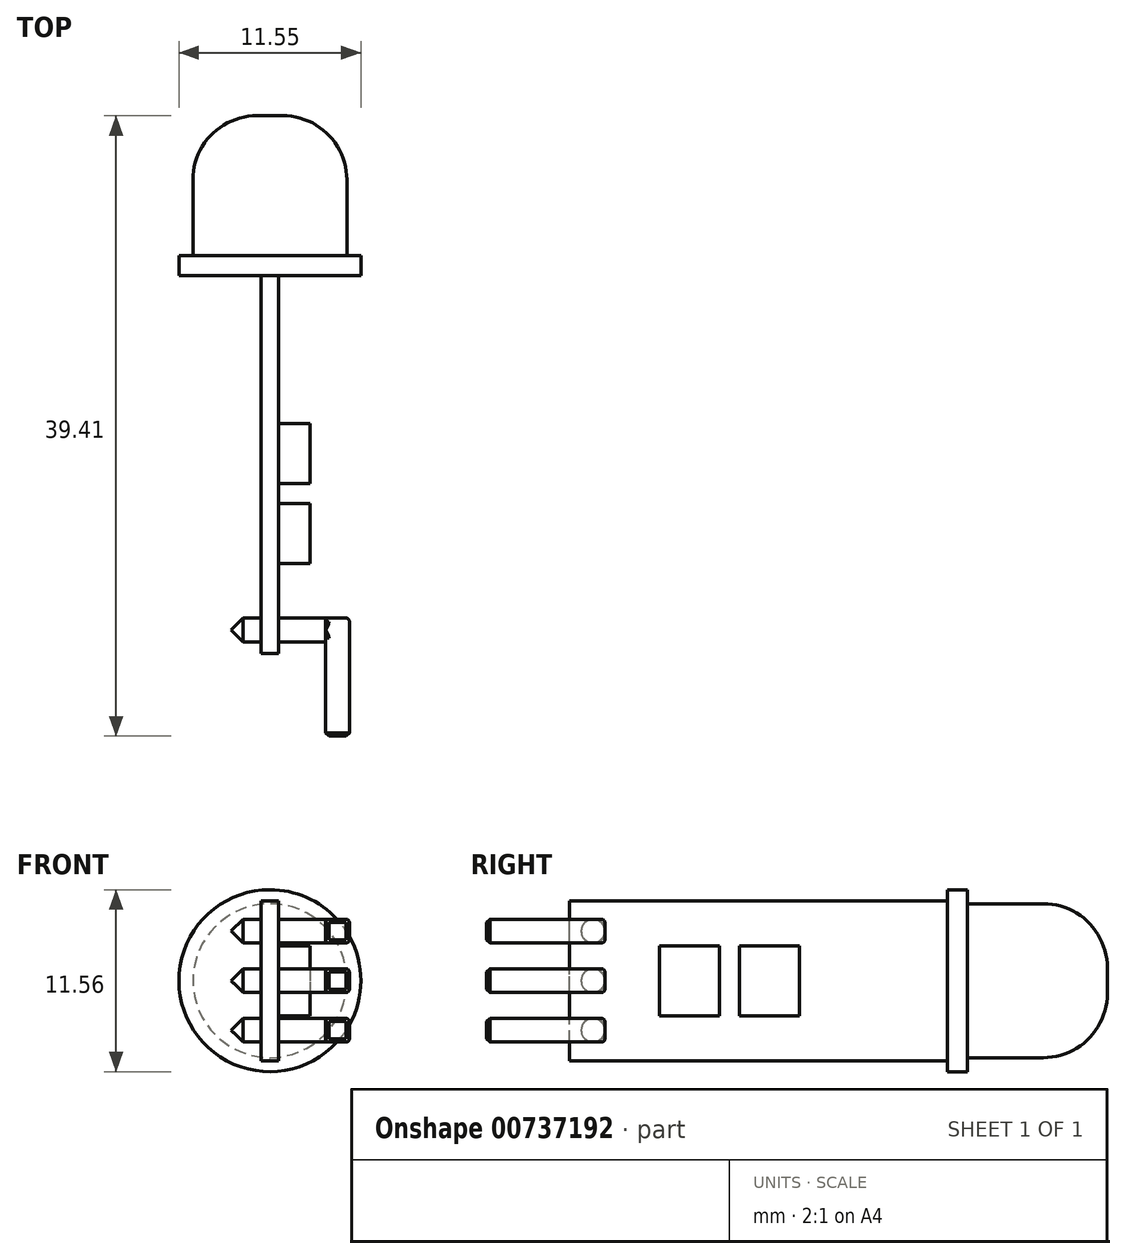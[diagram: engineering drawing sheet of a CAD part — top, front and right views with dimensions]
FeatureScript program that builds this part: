
annotation { "Feature Type Name" : "Feature", "Feature Type Description" : "" }
export const myFeature = defineFeature(function(context is Context, id is Id, definition is map)
    precondition{}
    {
        {
            var Q0;
            Q0=qCreatedBy(makeId("Right.planeOp"),FACE);
            var sketch = newSketch(context, id + "F0", { "sketchPlane" : qUnion([Q0])});
            skLineSegment(sketch, "E0.bottom", {"start": v(12, -5.08) * mm, "end": v(-12, -5.08) * mm});
            skLineSegment(sketch, "E0.top", {"start": v(12, 5.08) * mm, "end": v(-12, 5.08) * mm});
            skLineSegment(sketch, "E0.left", {"start": v(12, -5.08) * mm, "end": v(12, 5.08) * mm});
            skLineSegment(sketch, "E0.right", {"start": v(-12, -5.08) * mm, "end": v(-12, 5.08) * mm});
            skPoint(sketch, "E0.middle", {"position": v(0, 0) * mm});
            skSolve(sketch);
        }
        {
            var Q0;
            Q0 = qSketchRegion(id + "F0", true);
            extrude(context, id + "F1", {"entities" : qUnion([Q0]), "depth" : 1.1 * mm, "offsetDistance" : 25.4 * mm});
        }
        {
            var Q0;
            Q0=makeQuery(id+"F1.opExtrude","SWEPT_FACE",FACE,{"disambiguationData":[OSD([sQuery(id+"F0.wireOp",EDGE,"E0.left")])]});
            var sketch = newSketch(context, id + "F2", { "sketchPlane" : qUnion([Q0])});
            skLineSegment(sketch, "E1", {"start": v(-0.55, 5.08) * mm, "end": v(-0.55, -5.08) * mm});
            skCircle(sketch, "E2", {"center": v(-0.55, 0) * mm, "radius": 5.78 * mm});
            skSolve(sketch);
        }
        {
            var Q0;
            Q0 = qSketchRegion(id + "F2", true);
            extrude(context, id + "F3", {"entities" : qUnion([Q0]), "operationType" : NewBodyOperationType.ADD, "depth" : 1.27 * mm, "offsetDistance" : 25.4 * mm});
        }
        {
            var Q0;
            Q0=makeQuery(id+"F3.opExtrude","CAP_FACE",FACE,{"disambiguationData":[OSD([sQuery(id+"F2.wireOp",EDGE,"E2")])],"isStart":false});
            var sketch = newSketch(context, id + "F4", { "sketchPlane" : qUnion([Q0])});
            skCircle(sketch, "E3", {"center": v(-0.55, 0) * mm, "radius": 4.89 * mm});
            skSolve(sketch);
        }
        {
            var Q0;
            Q0 = qSketchRegion(id + "F4", true);
            extrude(context, id + "F5", {"entities" : qUnion([Q0]), "operationType" : NewBodyOperationType.ADD, "depth" : 10.16 * mm - 1.27 * mm, "offsetDistance" : 25.4 * mm});
        }
        {
            var Q0;
            Q0=makeQuery(id+"F5.opExtrude","CAP_EDGE",EDGE,{"disambiguationData":[OSD([sQuery(id+"F4.wireOp",EDGE,"E3")])],"isStart":false});
            fillet(context, id + "F6", {"entities" : qUnion([Q0]), "radius" : 4.06 * mm, "tangentPropagation" : true, "allowEdgeOverflow" : false});
        }
        {
            var Q0;
            Q0=makeQuery(id+"F1.opExtrude","CAP_FACE",FACE,{"disambiguationData":[OSD([sQuery(id+"F0.wireOp",EDGE,"E0.bottom"),sQuery(id+"F0.wireOp",EDGE,"E0.top"),sQuery(id+"F0.wireOp",EDGE,"E0.left"),sQuery(id+"F0.wireOp",EDGE,"E0.right")])],"isStart":false});
            var sketch = newSketch(context, id + "F7", { "sketchPlane" : qUnion([Q0])});
            skLineSegment(sketch, "E4.bottom", {"start": v(-2.48, 2.22) * mm, "end": v(-6.29, 2.22) * mm});
            skLineSegment(sketch, "E4.top", {"start": v(-2.48, -2.22) * mm, "end": v(-6.29, -2.22) * mm});
            skLineSegment(sketch, "E4.left", {"start": v(-2.48, 2.22) * mm, "end": v(-2.48, -2.22) * mm});
            skLineSegment(sketch, "E4.right", {"start": v(-6.29, 2.22) * mm, "end": v(-6.29, -2.22) * mm});
            skPoint(sketch, "E4.middle", {"position": v(-4.38, 0) * mm});
            skLineSegment(sketch, "E5.bottom", {"start": v(2.6, 2.22) * mm, "end": v(-1.2, 2.22) * mm});
            skLineSegment(sketch, "E5.top", {"start": v(2.6, -2.22) * mm, "end": v(-1.2, -2.22) * mm});
            skLineSegment(sketch, "E5.left", {"start": v(2.6, 2.22) * mm, "end": v(2.6, -2.22) * mm});
            skLineSegment(sketch, "E5.right", {"start": v(-1.2, 2.22) * mm, "end": v(-1.2, -2.22) * mm});
            skPoint(sketch, "E5.middle", {"position": v(0.7, 0) * mm});
            skSolve(sketch);
        }
        {
            var Q0;
            Q0 = qSketchRegion(id + "F7", true);
            extrude(context, id + "F8", {"entities" : qUnion([Q0]), "operationType" : NewBodyOperationType.ADD, "depth" : 2 * mm, "offsetDistance" : 25.4 * mm});
        }
        {
            var Q0;
            Q0=makeQuery(id+"F1.opExtrude","CAP_FACE",FACE,{"disambiguationData":[OSD([sQuery(id+"F0.wireOp",EDGE,"E0.bottom"),sQuery(id+"F0.wireOp",EDGE,"E0.top"),sQuery(id+"F0.wireOp",EDGE,"E0.left"),sQuery(id+"F0.wireOp",EDGE,"E0.right")])],"isStart":false});
            var sketch = newSketch(context, id + "F9", { "sketchPlane" : qUnion([Q0])});
            skCircle(sketch, "E6", {"center": v(-10.5, 0) * mm, "radius": 0.75 * mm});
            skCircle(sketch, "E7", {"center": v(-10.5, -3.15) * mm, "radius": 0.75 * mm});
            skCircle(sketch, "E8", {"center": v(-10.5, 3.15) * mm, "radius": 0.75 * mm});
            skPoint(sketch, "E9", {"position": v(-12, 0) * mm});
            skSolve(sketch);
        }
        {
            var Q0;
            Q0 = qSketchRegion(id + "F9", true);
            extrude(context, id + "F10", {"entities" : qUnion([Q0]), "operationType" : NewBodyOperationType.ADD, "endBound" : BoundingType.SYMMETRIC, "depth" : 6 * mm, "offsetDistance" : 25.4 * mm});
        }
        {
            var Q0;
            Q0=makeQuery(id+"F10.opExtrude","CAP_EDGE",EDGE,{"disambiguationData":[OSD([sQuery(id+"F9.wireOp",EDGE,"E8")])],"isStart":true});
            var Q1;
            Q1=makeQuery(id+"F10.opExtrude","CAP_EDGE",EDGE,{"disambiguationData":[OSD([sQuery(id+"F9.wireOp",EDGE,"E6")])],"isStart":true});
            var Q2;
            Q2=makeQuery(id+"F10.opExtrude","CAP_EDGE",EDGE,{"disambiguationData":[OSD([sQuery(id+"F9.wireOp",EDGE,"E7")])],"isStart":true});
            chamfer(context, id + "F11", {"entities" : qUnion([Q0, Q1, Q2]), "width" : 0.75 * mm, "tangentPropagation" : true});
        }
        {
            var Q0;
            Q0=makeQuery(id+"F10.opExtrude","CAP_FACE",FACE,{"disambiguationData":[OSD([sQuery(id+"F9.wireOp",EDGE,"E8")])],"isStart":false});
            var sketch = newSketch(context, id + "F12", { "sketchPlane" : qUnion([Q0])});
            skLineSegment(sketch, "E10.bottom", {"start": v(-17.25, 3.9) * mm, "end": v(-9.75, 3.9) * mm});
            skLineSegment(sketch, "E10.top", {"start": v(-17.25, 2.4) * mm, "end": v(-9.75, 2.4) * mm});
            skLineSegment(sketch, "E10.left", {"start": v(-17.25, 3.9) * mm, "end": v(-17.25, 2.4) * mm});
            skLineSegment(sketch, "E10.right", {"start": v(-9.75, 3.9) * mm, "end": v(-9.75, 2.4) * mm});
            skPoint(sketch, "E10.middle", {"position": v(-10.5, 3.15) * mm});
            skLineSegment(sketch, "E11.bottom", {"start": v(-17.25, 0.75) * mm, "end": v(-9.75, 0.75) * mm});
            skLineSegment(sketch, "E11.top", {"start": v(-17.25, -0.75) * mm, "end": v(-9.75, -0.75) * mm});
            skLineSegment(sketch, "E11.left", {"start": v(-17.25, 0.75) * mm, "end": v(-17.25, -0.75) * mm});
            skLineSegment(sketch, "E11.right", {"start": v(-9.75, 0.75) * mm, "end": v(-9.75, -0.75) * mm});
            skPoint(sketch, "E11.middle", {"position": v(-13.5, 0) * mm});
            skLineSegment(sketch, "E12.bottom", {"start": v(-17.25, -2.4) * mm, "end": v(-9.75, -2.4) * mm});
            skLineSegment(sketch, "E12.top", {"start": v(-17.25, -3.9) * mm, "end": v(-9.75, -3.9) * mm});
            skLineSegment(sketch, "E12.left", {"start": v(-17.25, -2.4) * mm, "end": v(-17.25, -3.9) * mm});
            skLineSegment(sketch, "E12.right", {"start": v(-9.75, -2.4) * mm, "end": v(-9.75, -3.9) * mm});
            skPoint(sketch, "E12.middle", {"position": v(-13.5, -3.15) * mm});
            skSolve(sketch);
        }
        {
            var Q0;
            Q0 = qSketchRegion(id + "F12", true);
            extrude(context, id + "F13", {"entities" : qUnion([Q0]), "operationType" : NewBodyOperationType.ADD, "depth" : 1.5 * mm, "offsetDistance" : 25.4 * mm});
        }
        {
            var Q0;
            {var subQ0=sQuery(id+"F12.wireOp",EDGE,"E12.right");var subQ1=sQuery(id+"F12.wireOp",EDGE,"E12.top");var subQ2=makeQuery(id+"F13.opExtrude","CAP_FACE",FACE,{"disambiguationData":[OSD([sQuery(id+"F12.wireOp",EDGE,"E12.bottom"),subQ1,sQuery(id+"F12.wireOp",EDGE,"E12.left"),subQ0])],"isStart":true});Q0=makeQuery(id+"F13.boolean.opBoolean","SPLIT",FACE,{"disambiguationData":[TD([makeQuery(id+"F10.opExtrude","SWEPT_FACE",FACE,{"disambiguationData":[OSD([sQuery(id+"F9.wireOp",EDGE,"E7")])]}),subQ2,makeQuery(id+"F13.opExtrude","SWEPT_FACE",FACE,{"disambiguationData":[OSD([subQ1])]}),makeQuery(id+"F13.opExtrude","SWEPT_FACE",FACE,{"disambiguationData":[OSD([subQ0])]})])],"derivedFrom":subQ2});}
            var Q1;
            {var subQ0=sQuery(id+"F12.wireOp",EDGE,"E12.right");var subQ1=sQuery(id+"F12.wireOp",EDGE,"E12.bottom");var subQ2=makeQuery(id+"F13.opExtrude","CAP_FACE",FACE,{"disambiguationData":[OSD([subQ1,sQuery(id+"F12.wireOp",EDGE,"E12.top"),sQuery(id+"F12.wireOp",EDGE,"E12.left"),subQ0])],"isStart":true});Q1=makeQuery(id+"F13.boolean.opBoolean","SPLIT",FACE,{"disambiguationData":[TD([makeQuery(id+"F10.opExtrude","SWEPT_FACE",FACE,{"disambiguationData":[OSD([sQuery(id+"F9.wireOp",EDGE,"E7")])]}),makeQuery(id+"F13.opExtrude","SWEPT_FACE",FACE,{"disambiguationData":[OSD([subQ1])]}),subQ2,makeQuery(id+"F13.opExtrude","SWEPT_FACE",FACE,{"disambiguationData":[OSD([subQ0])]})])],"derivedFrom":subQ2});}
            var Q2;
            {var subQ0=sQuery(id+"F12.wireOp",EDGE,"E11.right");var subQ1=sQuery(id+"F12.wireOp",EDGE,"E11.top");var subQ2=makeQuery(id+"F13.opExtrude","CAP_FACE",FACE,{"disambiguationData":[OSD([sQuery(id+"F12.wireOp",EDGE,"E11.bottom"),subQ1,sQuery(id+"F12.wireOp",EDGE,"E11.left"),subQ0])],"isStart":true});Q2=makeQuery(id+"F13.boolean.opBoolean","SPLIT",FACE,{"disambiguationData":[TD([makeQuery(id+"F10.opExtrude","SWEPT_FACE",FACE,{"disambiguationData":[OSD([sQuery(id+"F9.wireOp",EDGE,"E6")])]}),subQ2,makeQuery(id+"F13.opExtrude","SWEPT_FACE",FACE,{"disambiguationData":[OSD([subQ1])]}),makeQuery(id+"F13.opExtrude","SWEPT_FACE",FACE,{"disambiguationData":[OSD([subQ0])]})])],"derivedFrom":subQ2});}
            var Q3;
            {var subQ0=sQuery(id+"F12.wireOp",EDGE,"E11.bottom");var subQ1=sQuery(id+"F12.wireOp",EDGE,"E11.right");var subQ2=makeQuery(id+"F13.opExtrude","CAP_FACE",FACE,{"disambiguationData":[OSD([subQ0,sQuery(id+"F12.wireOp",EDGE,"E11.top"),sQuery(id+"F12.wireOp",EDGE,"E11.left"),subQ1])],"isStart":true});Q3=makeQuery(id+"F13.boolean.opBoolean","SPLIT",FACE,{"disambiguationData":[TD([makeQuery(id+"F10.opExtrude","SWEPT_FACE",FACE,{"disambiguationData":[OSD([sQuery(id+"F9.wireOp",EDGE,"E6")])]}),makeQuery(id+"F13.opExtrude","SWEPT_FACE",FACE,{"disambiguationData":[OSD([subQ0])]}),subQ2,makeQuery(id+"F13.opExtrude","SWEPT_FACE",FACE,{"disambiguationData":[OSD([subQ1])]})])],"derivedFrom":subQ2});}
            var Q4;
            {var subQ0=sQuery(id+"F12.wireOp",EDGE,"E10.right");var subQ1=sQuery(id+"F12.wireOp",EDGE,"E10.top");var subQ2=makeQuery(id+"F13.opExtrude","CAP_FACE",FACE,{"disambiguationData":[OSD([sQuery(id+"F12.wireOp",EDGE,"E10.bottom"),subQ1,sQuery(id+"F12.wireOp",EDGE,"E10.left"),subQ0])],"isStart":true});Q4=makeQuery(id+"F13.boolean.opBoolean","SPLIT",FACE,{"disambiguationData":[TD([makeQuery(id+"F10.opExtrude","SWEPT_FACE",FACE,{"disambiguationData":[OSD([sQuery(id+"F9.wireOp",EDGE,"E8")])]}),subQ2,makeQuery(id+"F13.opExtrude","SWEPT_FACE",FACE,{"disambiguationData":[OSD([subQ1])]}),makeQuery(id+"F13.opExtrude","SWEPT_FACE",FACE,{"disambiguationData":[OSD([subQ0])]})])],"derivedFrom":subQ2});}
            var Q5;
            {var subQ0=sQuery(id+"F12.wireOp",EDGE,"E10.right");var subQ1=sQuery(id+"F12.wireOp",EDGE,"E10.bottom");var subQ2=makeQuery(id+"F13.opExtrude","CAP_FACE",FACE,{"disambiguationData":[OSD([subQ1,sQuery(id+"F12.wireOp",EDGE,"E10.top"),sQuery(id+"F12.wireOp",EDGE,"E10.left"),subQ0])],"isStart":true});Q5=makeQuery(id+"F13.boolean.opBoolean","SPLIT",FACE,{"disambiguationData":[TD([makeQuery(id+"F10.opExtrude","SWEPT_FACE",FACE,{"disambiguationData":[OSD([sQuery(id+"F9.wireOp",EDGE,"E8")])]}),makeQuery(id+"F13.opExtrude","SWEPT_FACE",FACE,{"disambiguationData":[OSD([subQ1])]}),subQ2,makeQuery(id+"F13.opExtrude","SWEPT_FACE",FACE,{"disambiguationData":[OSD([subQ0])]})])],"derivedFrom":subQ2});}
            extrude(context, id + "F14", {"entities" : qUnion([Q0, Q1, Q2, Q3, Q4, Q5]), "operationType" : NewBodyOperationType.ADD, "oppositeDirection" : true, "depth" : 1.5 * mm, "offsetDistance" : 25.4 * mm});
        }
        {
            var Q0;
            Q0=makeQuery(id+"F13.opExtrude","SWEPT_EDGE",EDGE,{"disambiguationData":[OSD([sQuery(id+"F12.wireOp",EDGE,"E12.top"),sQuery(id+"F12.wireOp",EDGE,"E12.right")])]});
            var Q1;
            Q1=makeQuery(id+"F13.opExtrude","CAP_EDGE",EDGE,{"disambiguationData":[OSD([sQuery(id+"F12.wireOp",EDGE,"E12.top")])],"isStart":false});
            var Q2;
            {var subQ0=sQuery(id+"F12.wireOp",EDGE,"E12.left");var subQ1=sQuery(id+"F12.wireOp",EDGE,"E12.top");Q2=makeQuery(id+"F13.boolean.opBoolean","SPLIT",EDGE,{"disambiguationData":[TD([makeQuery(id+"F13.opExtrude","SWEPT_FACE",FACE,{"disambiguationData":[OSD([subQ0])]})])],"derivedFrom":makeQuery(id+"F13.opExtrude","CAP_EDGE",EDGE,{"disambiguationData":[OSD([subQ1])],"isStart":true})});}
            var Q3;
            {var subQ0=sQuery(id+"F12.wireOp",EDGE,"E12.right");var subQ1=sQuery(id+"F12.wireOp",EDGE,"E12.top");Q3=makeQuery(id+"F13.boolean.opBoolean","SPLIT",EDGE,{"disambiguationData":[TD([makeQuery(id+"F13.opExtrude","SWEPT_FACE",FACE,{"disambiguationData":[OSD([subQ0])]})])],"derivedFrom":makeQuery(id+"F13.opExtrude","CAP_EDGE",EDGE,{"disambiguationData":[OSD([subQ1])],"isStart":true})});}
            var Q4;
            {var subQ0=sQuery(id+"F12.wireOp",EDGE,"E12.right");var subQ1=sQuery(id+"F12.wireOp",EDGE,"E12.top");Q4=makeQuery(id+"F13.boolean.opBoolean","SPLIT",EDGE,{"disambiguationData":[TD([makeQuery(id+"F13.opExtrude","SWEPT_FACE",FACE,{"disambiguationData":[OSD([subQ1])]})])],"derivedFrom":makeQuery(id+"F13.opExtrude","CAP_EDGE",EDGE,{"disambiguationData":[OSD([subQ0])],"isStart":true})});}
            var Q5;
            {var subQ0=sQuery(id+"F12.wireOp",EDGE,"E12.right");var subQ1=sQuery(id+"F12.wireOp",EDGE,"E12.bottom");Q5=makeQuery(id+"F13.boolean.opBoolean","SPLIT",EDGE,{"disambiguationData":[TD([makeQuery(id+"F13.opExtrude","SWEPT_FACE",FACE,{"disambiguationData":[OSD([subQ1])]})])],"derivedFrom":makeQuery(id+"F13.opExtrude","CAP_EDGE",EDGE,{"disambiguationData":[OSD([subQ0])],"isStart":true})});}
            var Q6;
            Q6=makeQuery(id+"F13.opExtrude","SWEPT_EDGE",EDGE,{"disambiguationData":[OSD([sQuery(id+"F12.wireOp",EDGE,"E12.bottom"),sQuery(id+"F12.wireOp",EDGE,"E12.right")])]});
            var Q7;
            Q7=makeQuery(id+"F13.opExtrude","CAP_EDGE",EDGE,{"disambiguationData":[OSD([sQuery(id+"F12.wireOp",EDGE,"E12.right")])],"isStart":false});
            var Q8;
            Q8=makeQuery(id+"F13.opExtrude","CAP_EDGE",EDGE,{"disambiguationData":[OSD([sQuery(id+"F12.wireOp",EDGE,"E12.bottom")])],"isStart":false});
            var Q9;
            {var subQ0=sQuery(id+"F12.wireOp",EDGE,"E12.left");var subQ1=sQuery(id+"F12.wireOp",EDGE,"E12.bottom");Q9=makeQuery(id+"F13.boolean.opBoolean","SPLIT",EDGE,{"disambiguationData":[TD([makeQuery(id+"F13.opExtrude","SWEPT_FACE",FACE,{"disambiguationData":[OSD([subQ0])]})])],"derivedFrom":makeQuery(id+"F13.opExtrude","CAP_EDGE",EDGE,{"disambiguationData":[OSD([subQ1])],"isStart":true})});}
            var Q10;
            {var subQ0=sQuery(id+"F12.wireOp",EDGE,"E12.right");var subQ1=sQuery(id+"F12.wireOp",EDGE,"E12.bottom");Q10=makeQuery(id+"F13.boolean.opBoolean","SPLIT",EDGE,{"disambiguationData":[TD([makeQuery(id+"F13.opExtrude","SWEPT_FACE",FACE,{"disambiguationData":[OSD([subQ0])]})])],"derivedFrom":makeQuery(id+"F13.opExtrude","CAP_EDGE",EDGE,{"disambiguationData":[OSD([subQ1])],"isStart":true})});}
            var Q11;
            {var subQ0=sQuery(id+"F12.wireOp",EDGE,"E11.bottom");var subQ1=sQuery(id+"F12.wireOp",EDGE,"E11.right");Q11=makeQuery(id+"F13.boolean.opBoolean","SPLIT",EDGE,{"disambiguationData":[TD([makeQuery(id+"F13.opExtrude","SWEPT_FACE",FACE,{"disambiguationData":[OSD([subQ1])]})])],"derivedFrom":makeQuery(id+"F13.opExtrude","CAP_EDGE",EDGE,{"disambiguationData":[OSD([subQ0])],"isStart":true})});}
            var Q12;
            {var subQ0=sQuery(id+"F12.wireOp",EDGE,"E11.bottom");var subQ1=sQuery(id+"F12.wireOp",EDGE,"E11.right");Q12=makeQuery(id+"F13.boolean.opBoolean","SPLIT",EDGE,{"disambiguationData":[TD([makeQuery(id+"F13.opExtrude","SWEPT_FACE",FACE,{"disambiguationData":[OSD([subQ0])]})])],"derivedFrom":makeQuery(id+"F13.opExtrude","CAP_EDGE",EDGE,{"disambiguationData":[OSD([subQ1])],"isStart":true})});}
            var Q13;
            {var subQ0=sQuery(id+"F12.wireOp",EDGE,"E11.right");var subQ1=sQuery(id+"F12.wireOp",EDGE,"E11.top");Q13=makeQuery(id+"F13.boolean.opBoolean","SPLIT",EDGE,{"disambiguationData":[TD([makeQuery(id+"F13.opExtrude","SWEPT_FACE",FACE,{"disambiguationData":[OSD([subQ0])]})])],"derivedFrom":makeQuery(id+"F13.opExtrude","CAP_EDGE",EDGE,{"disambiguationData":[OSD([subQ1])],"isStart":true})});}
            var Q14;
            {var subQ0=sQuery(id+"F12.wireOp",EDGE,"E11.right");var subQ1=sQuery(id+"F12.wireOp",EDGE,"E11.top");Q14=makeQuery(id+"F13.boolean.opBoolean","SPLIT",EDGE,{"disambiguationData":[TD([makeQuery(id+"F13.opExtrude","SWEPT_FACE",FACE,{"disambiguationData":[OSD([subQ1])]})])],"derivedFrom":makeQuery(id+"F13.opExtrude","CAP_EDGE",EDGE,{"disambiguationData":[OSD([subQ0])],"isStart":true})});}
            var Q15;
            Q15=makeQuery(id+"F13.opExtrude","SWEPT_EDGE",EDGE,{"disambiguationData":[OSD([sQuery(id+"F12.wireOp",EDGE,"E11.bottom"),sQuery(id+"F12.wireOp",EDGE,"E11.right")])]});
            var Q16;
            Q16=makeQuery(id+"F13.opExtrude","SWEPT_EDGE",EDGE,{"disambiguationData":[OSD([sQuery(id+"F12.wireOp",EDGE,"E11.top"),sQuery(id+"F12.wireOp",EDGE,"E11.right")])]});
            var Q17;
            Q17=makeQuery(id+"F13.opExtrude","CAP_EDGE",EDGE,{"disambiguationData":[OSD([sQuery(id+"F12.wireOp",EDGE,"E11.right")])],"isStart":false});
            var Q18;
            Q18=makeQuery(id+"F13.opExtrude","CAP_EDGE",EDGE,{"disambiguationData":[OSD([sQuery(id+"F12.wireOp",EDGE,"E11.bottom")])],"isStart":false});
            var Q19;
            Q19=makeQuery(id+"F13.opExtrude","CAP_EDGE",EDGE,{"disambiguationData":[OSD([sQuery(id+"F12.wireOp",EDGE,"E11.top")])],"isStart":false});
            var Q20;
            Q20=makeQuery(id+"F13.opExtrude","CAP_EDGE",EDGE,{"disambiguationData":[OSD([sQuery(id+"F12.wireOp",EDGE,"E10.top")])],"isStart":false});
            var Q21;
            Q21=makeQuery(id+"F13.opExtrude","CAP_EDGE",EDGE,{"disambiguationData":[OSD([sQuery(id+"F12.wireOp",EDGE,"E10.bottom")])],"isStart":false});
            var Q22;
            Q22=makeQuery(id+"F13.opExtrude","CAP_EDGE",EDGE,{"disambiguationData":[OSD([sQuery(id+"F12.wireOp",EDGE,"E10.right")])],"isStart":false});
            var Q23;
            Q23=makeQuery(id+"F13.opExtrude","SWEPT_EDGE",EDGE,{"disambiguationData":[OSD([sQuery(id+"F12.wireOp",EDGE,"E10.bottom"),sQuery(id+"F12.wireOp",EDGE,"E10.right")])]});
            var Q24;
            {var subQ0=sQuery(id+"F12.wireOp",EDGE,"E10.right");var subQ1=sQuery(id+"F12.wireOp",EDGE,"E10.top");Q24=makeQuery(id+"F13.boolean.opBoolean","SPLIT",EDGE,{"disambiguationData":[TD([makeQuery(id+"F13.opExtrude","SWEPT_FACE",FACE,{"disambiguationData":[OSD([subQ1])]})])],"derivedFrom":makeQuery(id+"F13.opExtrude","CAP_EDGE",EDGE,{"disambiguationData":[OSD([subQ0])],"isStart":true})});}
            var Q25;
            {var subQ0=sQuery(id+"F12.wireOp",EDGE,"E10.right");var subQ1=sQuery(id+"F12.wireOp",EDGE,"E10.bottom");Q25=makeQuery(id+"F13.boolean.opBoolean","SPLIT",EDGE,{"disambiguationData":[TD([makeQuery(id+"F13.opExtrude","SWEPT_FACE",FACE,{"disambiguationData":[OSD([subQ1])]})])],"derivedFrom":makeQuery(id+"F13.opExtrude","CAP_EDGE",EDGE,{"disambiguationData":[OSD([subQ0])],"isStart":true})});}
            var Q26;
            {var subQ0=sQuery(id+"F12.wireOp",EDGE,"E10.right");var subQ1=sQuery(id+"F12.wireOp",EDGE,"E10.bottom");Q26=makeQuery(id+"F13.boolean.opBoolean","SPLIT",EDGE,{"disambiguationData":[TD([makeQuery(id+"F13.opExtrude","SWEPT_FACE",FACE,{"disambiguationData":[OSD([subQ0])]})])],"derivedFrom":makeQuery(id+"F13.opExtrude","CAP_EDGE",EDGE,{"disambiguationData":[OSD([subQ1])],"isStart":true})});}
            var Q27;
            {var subQ0=sQuery(id+"F12.wireOp",EDGE,"E10.left");var subQ1=sQuery(id+"F12.wireOp",EDGE,"E10.bottom");Q27=makeQuery(id+"F13.boolean.opBoolean","SPLIT",EDGE,{"disambiguationData":[TD([makeQuery(id+"F13.opExtrude","SWEPT_FACE",FACE,{"disambiguationData":[OSD([subQ0])]})])],"derivedFrom":makeQuery(id+"F13.opExtrude","CAP_EDGE",EDGE,{"disambiguationData":[OSD([subQ1])],"isStart":true})});}
            var Q28;
            Q28=makeQuery(id+"F13.opExtrude","SWEPT_EDGE",EDGE,{"disambiguationData":[OSD([sQuery(id+"F12.wireOp",EDGE,"E10.top"),sQuery(id+"F12.wireOp",EDGE,"E10.right")])]});
            var Q29;
            {var subQ0=sQuery(id+"F12.wireOp",EDGE,"E10.right");var subQ1=sQuery(id+"F12.wireOp",EDGE,"E10.top");Q29=makeQuery(id+"F13.boolean.opBoolean","SPLIT",EDGE,{"disambiguationData":[TD([makeQuery(id+"F13.opExtrude","SWEPT_FACE",FACE,{"disambiguationData":[OSD([subQ0])]})])],"derivedFrom":makeQuery(id+"F13.opExtrude","CAP_EDGE",EDGE,{"disambiguationData":[OSD([subQ1])],"isStart":true})});}
            var Q30;
            {var subQ0=sQuery(id+"F12.wireOp",EDGE,"E11.left");var subQ1=sQuery(id+"F12.wireOp",EDGE,"E11.top");Q30=makeQuery(id+"F13.boolean.opBoolean","SPLIT",EDGE,{"disambiguationData":[TD([makeQuery(id+"F13.opExtrude","SWEPT_FACE",FACE,{"disambiguationData":[OSD([subQ0])]})])],"derivedFrom":makeQuery(id+"F13.opExtrude","CAP_EDGE",EDGE,{"disambiguationData":[OSD([subQ1])],"isStart":true})});}
            var Q31;
            {var subQ0=sQuery(id+"F12.wireOp",EDGE,"E11.left");var subQ1=sQuery(id+"F12.wireOp",EDGE,"E11.bottom");Q31=makeQuery(id+"F13.boolean.opBoolean","SPLIT",EDGE,{"disambiguationData":[TD([makeQuery(id+"F13.opExtrude","SWEPT_FACE",FACE,{"disambiguationData":[OSD([subQ0])]})])],"derivedFrom":makeQuery(id+"F13.opExtrude","CAP_EDGE",EDGE,{"disambiguationData":[OSD([subQ1])],"isStart":true})});}
            var Q32;
            {var subQ0=sQuery(id+"F12.wireOp",EDGE,"E10.left");var subQ1=sQuery(id+"F12.wireOp",EDGE,"E10.top");Q32=makeQuery(id+"F13.boolean.opBoolean","SPLIT",EDGE,{"disambiguationData":[TD([makeQuery(id+"F13.opExtrude","SWEPT_FACE",FACE,{"disambiguationData":[OSD([subQ0])]})])],"derivedFrom":makeQuery(id+"F13.opExtrude","CAP_EDGE",EDGE,{"disambiguationData":[OSD([subQ1])],"isStart":true})});}
            fillet(context, id + "F15", {"entities" : qUnion([Q0, Q1, Q2, Q3, Q4, Q5, Q6, Q7, Q8, Q9, Q10, Q11, Q12, Q13, Q14, Q15, Q16, Q17, Q18, Q19, Q20, Q21, Q22, Q23, Q24, Q25, Q26, Q27, Q28, Q29, Q30, Q31, Q32]), "radius" : 0.2 * mm, "tangentPropagation" : true, "allowEdgeOverflow" : false});
        }
        {
            var Q0;
            Q0=makeQuery(id+"F13.opExtrude","SWEPT_FACE",FACE,{"disambiguationData":[OSD([sQuery(id+"F12.wireOp",EDGE,"E10.left")])]});
            var Q1;
            Q1=makeQuery(id+"F13.opExtrude","SWEPT_FACE",FACE,{"disambiguationData":[OSD([sQuery(id+"F12.wireOp",EDGE,"E11.left")])]});
            var Q2;
            Q2=makeQuery(id+"F13.opExtrude","SWEPT_FACE",FACE,{"disambiguationData":[OSD([sQuery(id+"F12.wireOp",EDGE,"E12.left")])]});
            chamfer(context, id + "F16", {"entities" : qUnion([Q0, Q1, Q2]), "width" : 0.2 * mm, "tangentPropagation" : true});
        }
    });
